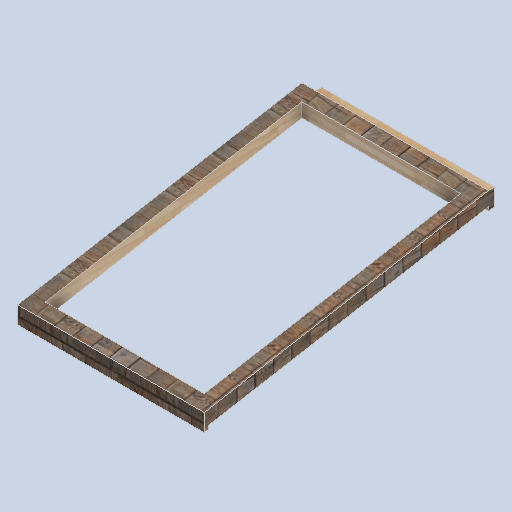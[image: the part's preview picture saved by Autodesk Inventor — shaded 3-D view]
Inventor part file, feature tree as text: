
AUTODESK INVENTOR PART (.ipt)
format: ipt  version: 2024.2 (Build 282272000, 272)  size: 424,960 bytes
history: native  units: mm
features: sketch x8, plane x4, extrude x4, loft x1, other x1, projected_geometry x1
ambient origin geometry x8: Origin, YZ Plane, XZ Plane, XY Plane, X Axis, Y Axis, Z Axis, Center Point
bodies: Body1 (feature_tree)
feature tree (19):
  sketch  "Sketch19"  dims[d29=200.0mm d30=200.0mm]
  plane  "Work Plane17"
  sketch  "Sketch20"  dims[d31=100.0mm d32=150.0mm]
  extrude  "Extrusion4"  Depth=200.0mm
  plane  "Work Plane18"
  sketch  "Sketch22"  dims[d33=2500.0mm d34=51.0mm d35=0.0mm]
  plane  "Work Plane19"
  sketch  "Sketch23"  dims[d36=0.0mm d37=13.962634mm]
  loft  "Loft2"
  extrude  "Extrusion5"  Depth=51.0mm TaperAngle=0.0deg
  plane  "Work Plane20"
  extrude  "Extrusion6"  Depth=13.962634mm
  extrude  "Extrusion7"  TaperAngle=0.0deg  [1 undecoded]
  sketch  "Sketch24"  dims[d38=13.962634mm d39=0.0mm d40=90.0deg]
  other  "Edges1"
  sketch  "Sketch25"  dims[d41=0.0mm d42=90.0deg]
  projected_geometry  "Projected Loop2"
  sketch  "Sketch26"  dims[d43=90.0deg]
  sketch  "Sketch27"  dims[d44=2450.0mm d45=29.670597mm d46=0.0mm d47=0.0mm d48=180.0deg d49=120.0mm d50=120.0mm d51=120.0mm d52=0.0mm d53=0.0mm d54=120.0mm d55=0.0mm d56=0.0mm]
note: 1 required parameter value undecoded (feature->parameter linkage not recoverable at this tier; creation-order binding heuristic only, values carry confidence <= 0.55)
